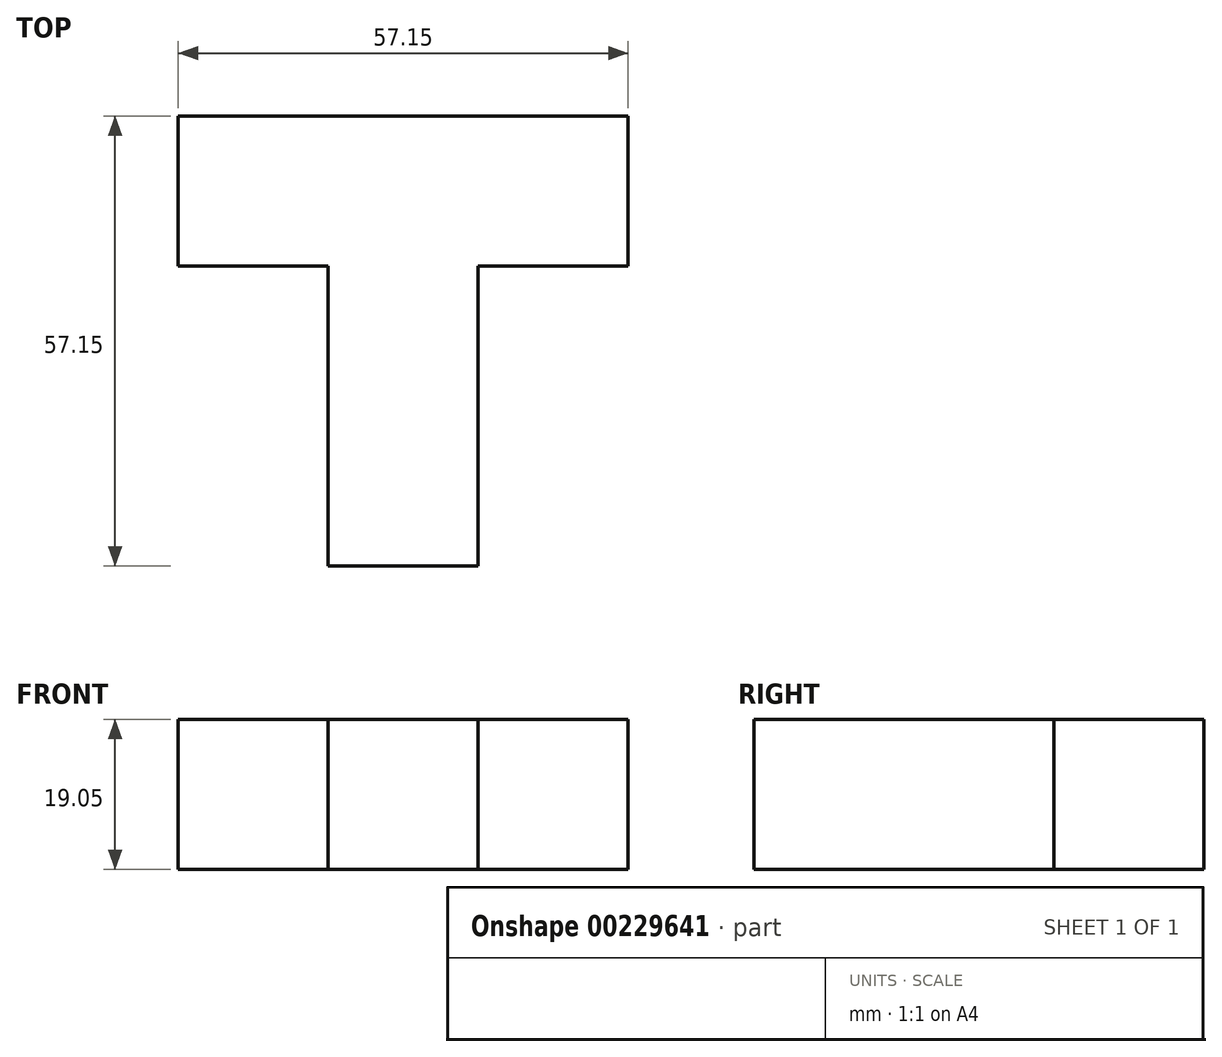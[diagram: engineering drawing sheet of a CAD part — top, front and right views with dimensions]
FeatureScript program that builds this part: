
annotation { "Feature Type Name" : "Feature", "Feature Type Description" : "" }
export const myFeature = defineFeature(function(context is Context, id is Id, definition is map)
    precondition{}
    {
        {
            var Q0;
            Q0=qCreatedBy(makeId("Top.planeOp"),FACE);
            var sketch = newSketch(context, id + "F0", { "sketchPlane" : qUnion([Q0])});
            skLineSegment(sketch, "E0", {"start": v(0, 0) * mm, "end": v(0, 38.1) * mm});
            skLineSegment(sketch, "E1", {"start": v(0, 38.1) * mm, "end": v(19.05, 38.1) * mm});
            skLineSegment(sketch, "E2", {"start": v(19.05, 38.1) * mm, "end": v(19.05, 57.15) * mm});
            skLineSegment(sketch, "E3", {"start": v(19.05, 57.15) * mm, "end": v(-38.1, 57.15) * mm});
            skLineSegment(sketch, "E4", {"start": v(-38.1, 57.15) * mm, "end": v(-38.1, 38.1) * mm});
            skLineSegment(sketch, "E5", {"start": v(-38.1, 38.1) * mm, "end": v(-19.05, 38.1) * mm});
            skLineSegment(sketch, "E6", {"start": v(-19.05, 38.1) * mm, "end": v(-19.05, 0) * mm});
            skLineSegment(sketch, "E7", {"start": v(-19.05, 0) * mm, "end": v(0, 0) * mm});
            skSolve(sketch);
        }
        {
            var Q0;
            Q0=makeQuery(id+"F0.imprint","IMPRINT",FACE,{"disambiguationData":[TD([[makeQuery(id+"F0.imprint","IMPRINT",EDGE,{"derivedFrom":sQuery(id+"F0.wireOp",EDGE,"E0")}),1.0]])]});
            extrude(context, id + "F1", {"entities" : qUnion([Q0]), "depth" : 19.05 * mm});
        }
    });
